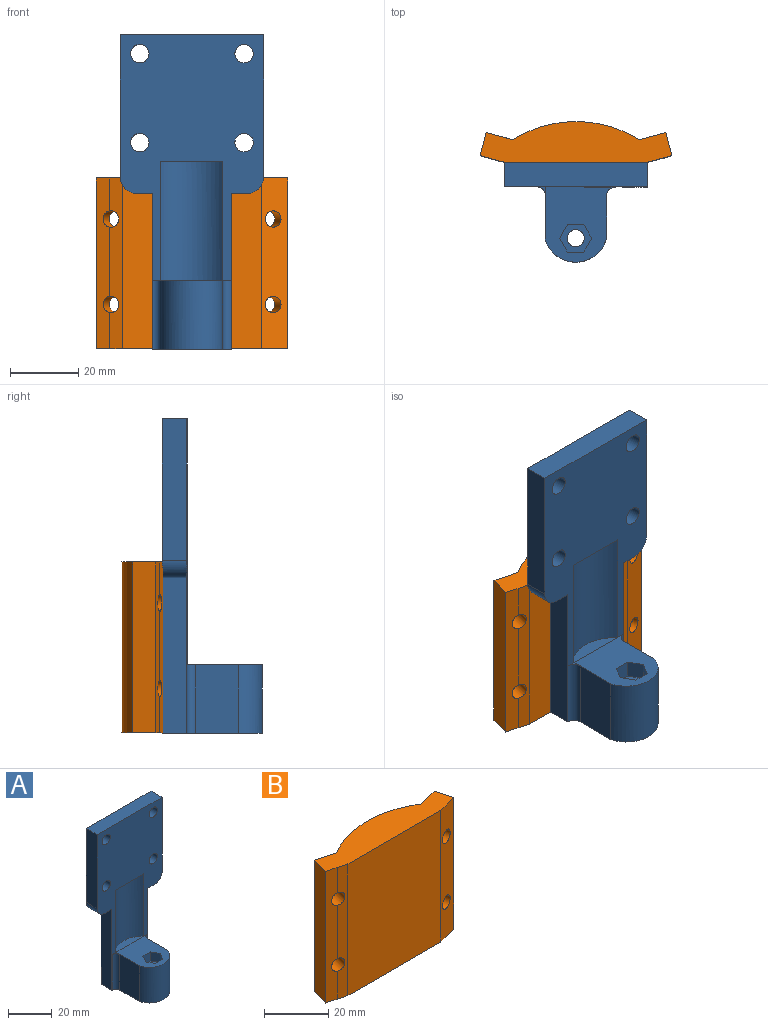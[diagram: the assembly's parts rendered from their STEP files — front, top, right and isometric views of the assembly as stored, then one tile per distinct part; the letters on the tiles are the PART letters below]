
ASSEMBLY  parts=2 mates=1
PART A: 43 faces, bbox 42x29.1x92 mm
  f0: cylinder r=2.5mm len=10mm, axis (0,0,-1), area 157.1mm2, adj f28,f29
  f1: plane 22.03x20.44mm, normal (0,0,1), area 306.4mm2, adj f5,f11,f12,f13,f30,f31,f32,f33
  f2: plane 29.07x23.15mm, normal (0,0,-1), area 470.6mm2, adj f5,f6,f7,f8,f9,f11,f12,f13
  f3: plane 41.47x7.07mm, normal (-1,0,0), area 293.1mm2, adj f5,f6,f10,f40
  f4: plane 41.47x7.07mm, normal (1,0,0), area 293.1mm2, adj f5,f9,f10,f39
  f5: plane 92x42mm, normal (0,-1,0), area 1803.9mm2, adj f1,f2,f3,f4,f10,f14,f15,f16
  f6: plane 92.04x12.1mm, normal (0.01,1,0), area 629.4mm2, adj f2,f3,f7,f10,f18,f19,f20,f21
  f7: plane 92x0.94mm, normal (0,1,0), area 86.1mm2, adj f2,f6,f8,f10
  f8: plane 92x17mm, normal (0,1,0), area 1564mm2, adj f2,f7,f9,f10
  f9: plane 92x12mm, normal (0,1,0), area 623.8mm2, adj f2,f4,f8,f10,f14,f15,f16,f17
  f10: plane 42x7.07mm, normal (0,0,1), area 295.8mm2, adj f3,f4,f5,f6,f7,f8,f9
  f11: plane 20x12.5mm, normal (1,0,0), area 250mm2, adj f1,f2,f12,f41
  f12: cylinder r=9.29mm len=20mm, axis (0,0,-1), area 486.1mm2, adj f1,f2,f11,f13
  f13: plane 20x15.24mm, normal (-1,0,0), area 254.8mm2, adj f1,f2,f12,f38,f42
  f14: cylinder r=2.7mm len=7.07mm, axis (0,-1,0), area 119.9mm2, adj f5,f9
  f15: plane 7.07x4.43mm, normal (0,0,-1), area 31.3mm2, adj f5,f9,f16,f39
  f16: plane 45.53x7.07mm, normal (1,0,0), area 321.8mm2, adj f2,f5,f9,f15
  f17: cylinder r=2.7mm len=7.07mm, axis (0,-1,0), area 119.9mm2, adj f5,f9
  f18: cylinder r=2.7mm len=7.04mm, axis (0,-1,0), area 119.2mm2, adj f5,f6
  f19: cylinder r=2.7mm len=7.04mm, axis (0,-1,0), area 119.2mm2, adj f5,f6
  f20: plane 7.04x4.43mm, normal (0,0,-1), area 31.1mm2, adj f5,f6,f21,f40
  f21: plane 45.53x7.02mm, normal (-1,0,0), area 319.4mm2, adj f2,f5,f6,f20
  f22: plane 5x4.7mm, normal (0,-1,0), area 23.5mm2, adj f2,f23,f27,f28
  f23: plane 5x4.07mm, normal (-0.87,-0.5,0), area 23.5mm2, adj f2,f22,f24,f28
  f24: plane 5x4.07mm, normal (-0.87,0.5,0), area 23.5mm2, adj f2,f23,f25,f28
  f25: plane 5x4.7mm, normal (0,1,0), area 23.5mm2, adj f2,f24,f26,f28
  f26: plane 5x4.07mm, normal (0.87,0.5,0), area 23.5mm2, adj f2,f25,f27,f28
  f27: plane 5x4.07mm, normal (0.87,-0.5,0), area 23.5mm2, adj f2,f22,f26,f28
  f28: plane 9.4x8.14mm, normal (0,0,-1), area 37.7mm2, adj f0,f22,f23,f24,f25,f26,f27
  f29: plane 9.4x8.14mm, normal (0,0,1), area 37.7mm2, adj f0,f30,f31,f32,f33,f34,f35
  f30: plane 5x4.07mm, normal (0.87,0.5,0), area 23.5mm2, adj f1,f29,f31,f35
  f31: plane 5x4.7mm, normal (0,1,0), area 23.5mm2, adj f1,f29,f30,f32
  f32: plane 5x4.07mm, normal (-0.87,0.5,0), area 23.5mm2, adj f1,f29,f31,f33
  f33: plane 5x4.07mm, normal (-0.87,-0.5,0), area 23.5mm2, adj f1,f29,f32,f34
  f34: plane 5x4.7mm, normal (0,-1,0), area 23.5mm2, adj f1,f29,f33,f35
  f35: plane 5x4.07mm, normal (0.87,-0.5,0), area 23.5mm2, adj f1,f29,f30,f34
  f36: plane 18.31x4mm, normal (0,0,-1), area 50.6mm2, adj f5,f37
  f37: cylinder r=12.47mm len=35mm, axis (0,0,-1), area 719.4mm2, adj f5,f36,f38
  f38: plane 20.46x6.52mm, normal (0,0,1), area 52mm2, adj f1,f5,f13,f37,f42
  f39: cylinder r=5mm len=7.07mm, axis (0,-1,0), area 55.5mm2, adj f4,f5,f9,f15
  f40: cylinder r=5mm len=7.07mm, axis (0,-1,0), area 55.4mm2, adj f3,f5,f6,f20
  f41: cylinder r=2.5mm len=20mm, axis (0,0,1), area 78.5mm2, adj f1,f2,f5,f11
  f42: cylinder r=2.5mm len=20mm, axis (0,0,-1), area 78.5mm2, adj f2,f5,f13,f38
PART B: 15 faces, bbox 56.1x12.1x50 mm
  f0: plane 50x7.73mm, normal (-0.26,0.97,0), area 363.8mm2, adj f1,f8,f9,f10,f13,f14
  f1: cylinder r=35.05mm len=50mm, axis (0,0,1), area 1952.4mm2, adj f0,f2,f9,f10
  f2: plane 50x7.73mm, normal (0.26,0.97,0), area 363.8mm2, adj f1,f3,f9,f10,f11,f12
  f3: plane 50x6.76mm, normal (-0.97,0.26,0), area 350mm2, adj f2,f4,f9,f10
  f4: plane 50x3.94mm, normal (-0.26,-0.97,0), area 190mm2, adj f3,f5,f9,f10,f11,f12
  f5: plane 50x3.78mm, normal (-0.26,-0.97,0), area 173.8mm2, adj f4,f6,f9,f10,f11,f12
  f6: plane 50x40.68mm, normal (0,-1,0), area 2034.2mm2, adj f5,f7,f9,f10
  f7: plane 50x7.73mm, normal (0.26,-0.97,0), area 363.8mm2, adj f6,f8,f9,f10,f13,f14
  f8: plane 50x6.76mm, normal (0.97,0.26,0), area 350mm2, adj f0,f7,f9,f10
  f9: plane 56.14x12.06mm, normal (0,0,-1), area 507.8mm2, adj f0,f1,f2,f3,f4,f5,f6,f7
  f10: plane 56.14x12.06mm, normal (0,0,1), area 507.8mm2, adj f0,f1,f2,f3,f4,f5,f6,f7
  f11: cylinder r=2.4mm len=8mm, axis (-0.26,-0.97,0), area 105.6mm2, adj f2,f4,f5
  f12: cylinder r=2.4mm len=8mm, axis (-0.26,-0.97,0), area 105.6mm2, adj f2,f4,f5
  f13: cylinder r=2.4mm len=8mm, axis (0.26,-0.97,0), area 105.6mm2, adj f0,f7
  f14: cylinder r=2.4mm len=8mm, axis (0.26,-0.97,0), area 105.6mm2, adj f0,f7
PLACE A rot(axis=(0,0,-1),0.2deg) t=(5.16,4.83,-0.66)mm
PLACE B t=(5.18,8.28,-8.29)mm
MATE planar A.f8 <-> B.f6  axis (0,1,0) through (5.18,11.82,-0.39)mm
